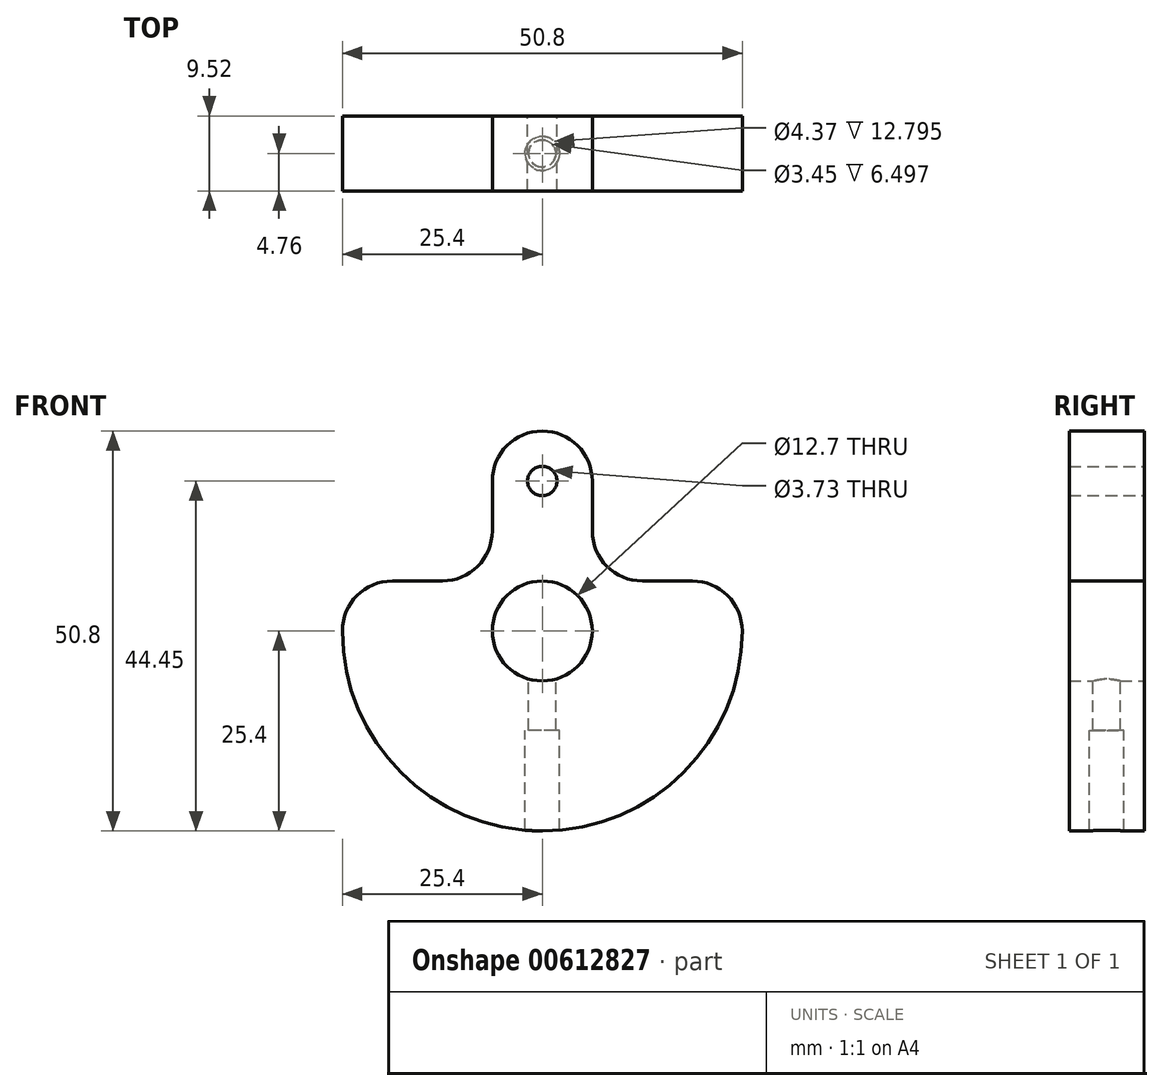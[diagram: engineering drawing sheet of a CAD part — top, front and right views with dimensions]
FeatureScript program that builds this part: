
annotation { "Feature Type Name" : "Feature", "Feature Type Description" : "" }
export const myFeature = defineFeature(function(context is Context, id is Id, definition is map)
    precondition{}
    {
        {
            var Q0;
            Q0=qCreatedBy(makeId("Front.planeOp"),FACE);
            var sketch = newSketch(context, id + "F0", { "sketchPlane" : qUnion([Q0])});
            skArc(sketch, "E0", {"start": v(25.4, 0) * mm, "mid": v(0, -25.4) * mm, "end": v(-25.4, 0) * mm});
            skCircle(sketch, "E1", {"center": v(0, 0) * mm, "radius": 6.35 * mm});
            skCircle(sketch, "E2", {"center": v(0, 19.05) * mm, "radius": 1.87 * mm});
            skArc(sketch, "E3", {"start": v(-6.35, 19.05) * mm, "mid": v(0, 25.4) * mm, "end": v(6.35, 19.05) * mm});
            skLineSegment(sketch, "E4", {"start": v(-6.35, 19.05) * mm, "end": v(-6.35, 12.7) * mm});
            skLineSegment(sketch, "E5", {"start": v(6.35, 19.05) * mm, "end": v(6.35, 12.7) * mm});
            skLineSegment(sketch, "E6", {"start": v(-12.7, 6.35) * mm, "end": v(-19.05, 6.35) * mm});
            skLineSegment(sketch, "E7", {"start": v(12.7, 6.35) * mm, "end": v(19.05, 6.35) * mm});
            skArc(sketch, "E8", {"start": v(25.4, 0) * mm, "mid": v(23.54, 4.5) * mm, "end": v(19.05, 6.35) * mm});
            skArc(sketch, "E9", {"start": v(-25.4, 0) * mm, "mid": v(-23.54, 4.5) * mm, "end": v(-19.05, 6.35) * mm});
            skArc(sketch, "E10", {"start": v(-6.35, 12.7) * mm, "mid": v(-8.2, 8.2) * mm, "end": v(-12.7, 6.35) * mm});
            skArc(sketch, "E11", {"start": v(6.35, 12.7) * mm, "mid": v(8.2, 8.2) * mm, "end": v(12.7, 6.35) * mm});
            skPoint(sketch, "E12.orphan", {"position": v(-6.35, 6.35) * mm});
            skPoint(sketch, "E13.orphan", {"position": v(6.35, 6.35) * mm});
            skSolve(sketch);
        }
        {
            var Q0;
            Q0=qSketchRegion(id+"F0",true);
            extrude(context, id + "F1", {"entities" : qUnion([Q0]), "depth" : 9.52 * mm, "symmetric" : true});
        }
        {
            var Q0;
            Q0=qCreatedBy(makeId("Top.planeOp"),FACE);
            cPlane(context, id + "F2", {"entities" : qUnion([Q0]), "cplaneType" : CPlaneType.OFFSET, "offset" : 25.4 * mm, "oppositeDirection" : true, "width" : 152.4 * mm, "height" : 152.4 * mm});
        }
        {
            var Q0;
            Q0=qCreatedBy(id+"F2.planeOp",FACE);
            var sketch = newSketch(context, id + "F3", { "sketchPlane" : qUnion([Q0])});
            skPoint(sketch, "E14", {"position": v(0, 0) * mm});
            skSolve(sketch);
        }
        {
            var Q0;
            Q0=sQuery(id+"F3.wireOp",VERTEX,"E14");
            var Q1;
            Q1=makeQuery(id+"F1.opExtrude","SWEPT_BODY",BODY,{"disambiguationData":[OSD([sQuery(id+"F0.wireOp",EDGE,"E0"),sQuery(id+"F0.wireOp",EDGE,"E1"),sQuery(id+"F0.wireOp",EDGE,"E2"),sQuery(id+"F0.wireOp",EDGE,"E3"),sQuery(id+"F0.wireOp",EDGE,"E4"),sQuery(id+"F0.wireOp",EDGE,"E5"),sQuery(id+"F0.wireOp",EDGE,"E6"),sQuery(id+"F0.wireOp",EDGE,"E7"),sQuery(id+"F0.wireOp",EDGE,"E8"),sQuery(id+"F0.wireOp",EDGE,"E9"),sQuery(id+"F0.wireOp",EDGE,"E10"),sQuery(id+"F0.wireOp",EDGE,"E11")])]});
            hole(context, id + "F4", {"style" : HoleStyle.C_BORE, "holeDiameter" : 3.45 * mm, "cBoreDiameter" : 4.37 * mm, "cBoreDepth" : 12.7 * mm, "endStyle" : HoleEndStyle.BLIND, "oppositeDirection" : true, "holeDepth" : 25.4 * mm, "locations" : qUnion([Q0]), "scope" : qUnion([Q1])});
        }
    });
